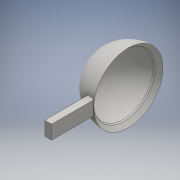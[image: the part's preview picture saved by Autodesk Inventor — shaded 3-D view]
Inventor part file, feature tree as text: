
AUTODESK INVENTOR PART (.ipt)
format: ipt  version: 2016 (Build 200138000, 138)  size: 152,064 bytes
history: native  units: mm
features: sketch x2, other x1, revolve x1, fillet x1, extrude x1
ambient origin geometry x8: Origin, YZ Plane, XZ Plane, XY Plane, X Axis, Y Axis, Z Axis, Center Point
bodies: Body1 (feature_tree)
feature tree (6):
  other  "ソリッド1"
  revolve  "回転1"
  fillet  "フィレット1"  Radius=25.0mm
  extrude  "押し出し1"  Depth=25.0mm
  sketch  "スケッチ1"
  sketch  "スケッチ2"
